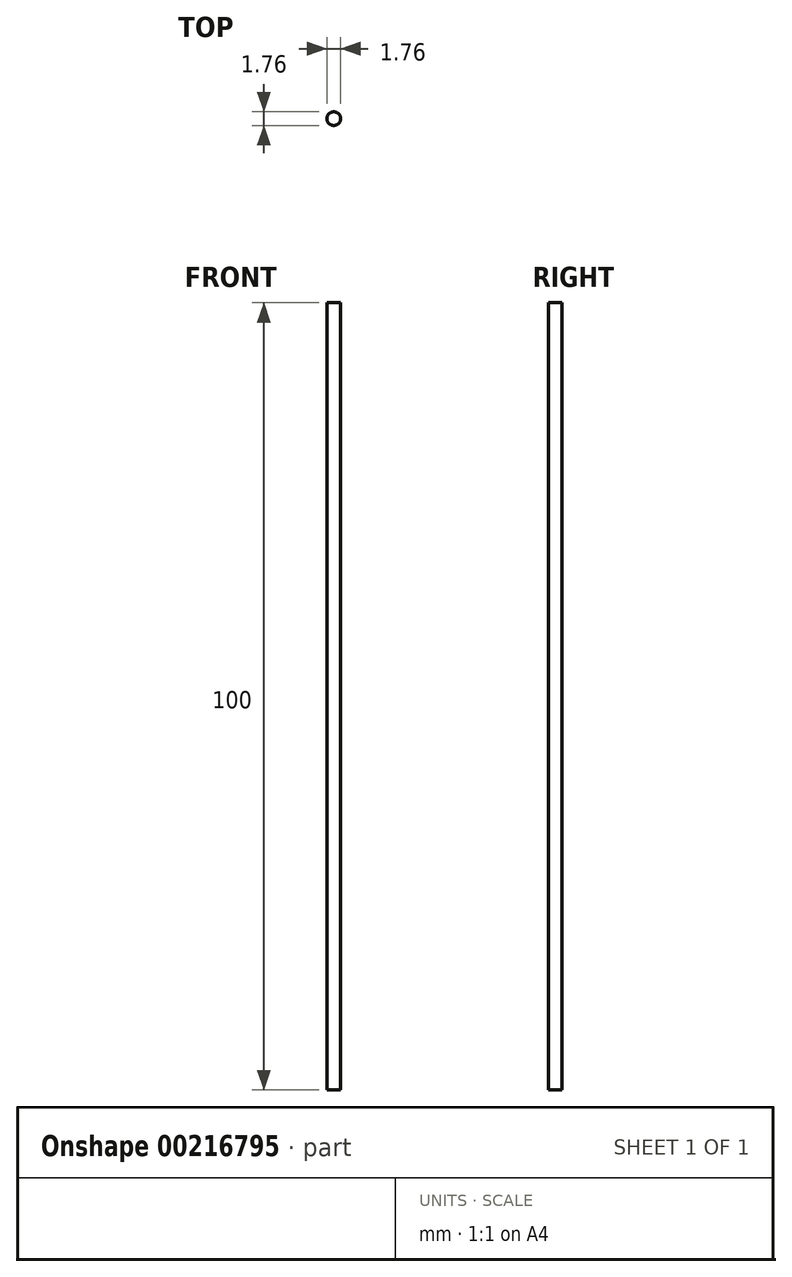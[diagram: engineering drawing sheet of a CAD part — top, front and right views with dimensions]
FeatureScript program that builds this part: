
annotation { "Feature Type Name" : "Feature", "Feature Type Description" : "" }
export const myFeature = defineFeature(function(context is Context, id is Id, definition is map)
    precondition{}
    {
        {
            var Q0;
            Q0=qCreatedBy(makeId("Top.planeOp"),FACE);
            var sketch = newSketch(context, id + "F0", { "sketchPlane" : qUnion([Q0])});
            skCircle(sketch, "E0", {"center": v(0, 0) * mm, "radius": 0.88 * mm});
            skSolve(sketch);
        }
        {
            var Q0;
            Q0 = qSketchRegion(id + "F0", true);
            extrude(context, id + "F1", {"entities" : qUnion([Q0]), "depth" : 100 * mm});
        }
    });
